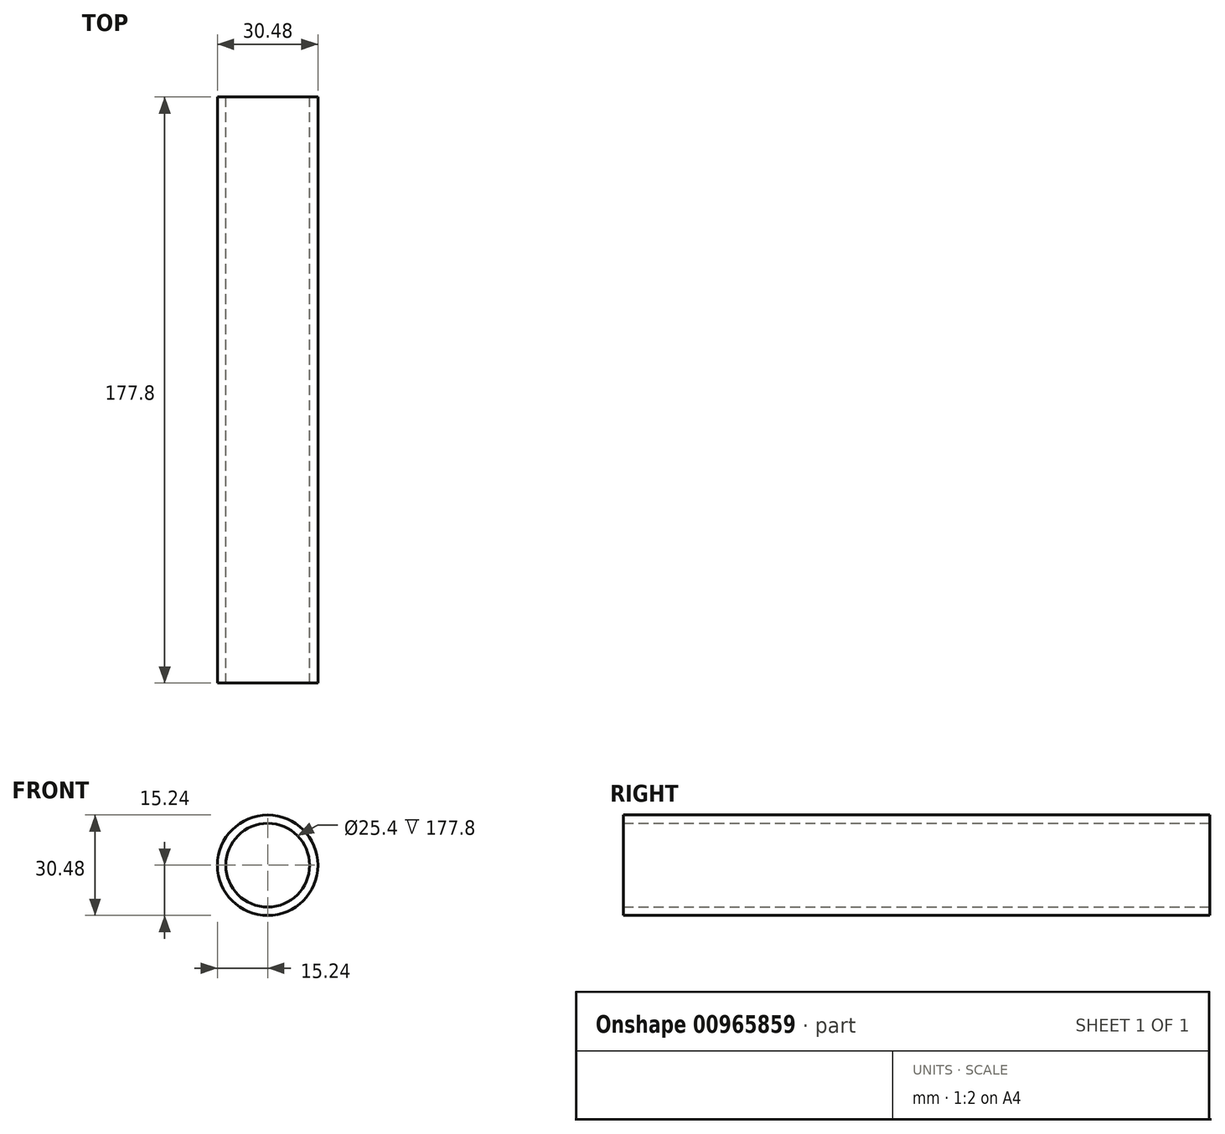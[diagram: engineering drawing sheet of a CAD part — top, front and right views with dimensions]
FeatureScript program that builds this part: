
annotation { "Feature Type Name" : "Feature", "Feature Type Description" : "" }
export const myFeature = defineFeature(function(context is Context, id is Id, definition is map)
    precondition{}
    {
        {
            var Q0;
            Q0=qCreatedBy(makeId("Front.planeOp"),FACE);
            var sketch = newSketch(context, id + "F0", { "sketchPlane" : qUnion([Q0])});
            skCircle(sketch, "E0", {"center": v(0, 0) * mm, "radius": 15.24 * mm});
            skCircle(sketch, "E1", {"center": v(0, 0) * mm, "radius": 12.7 * mm});
            skSolve(sketch);
        }
        {
            var Q0;
            Q0=makeQuery(id+"F0.imprint","IMPRINT",FACE,{"disambiguationData":[TD([[makeQuery(id+"F0.imprint","IMPRINT",EDGE,{"derivedFrom":sQuery(id+"F0.wireOp",EDGE,"E0")}),1.0]])]});
            extrude(context, id + "F1", {"entities" : qUnion([Q0]), "depth" : 177.8 * mm, "offsetDistance" : 25.4 * mm});
        }
    });
